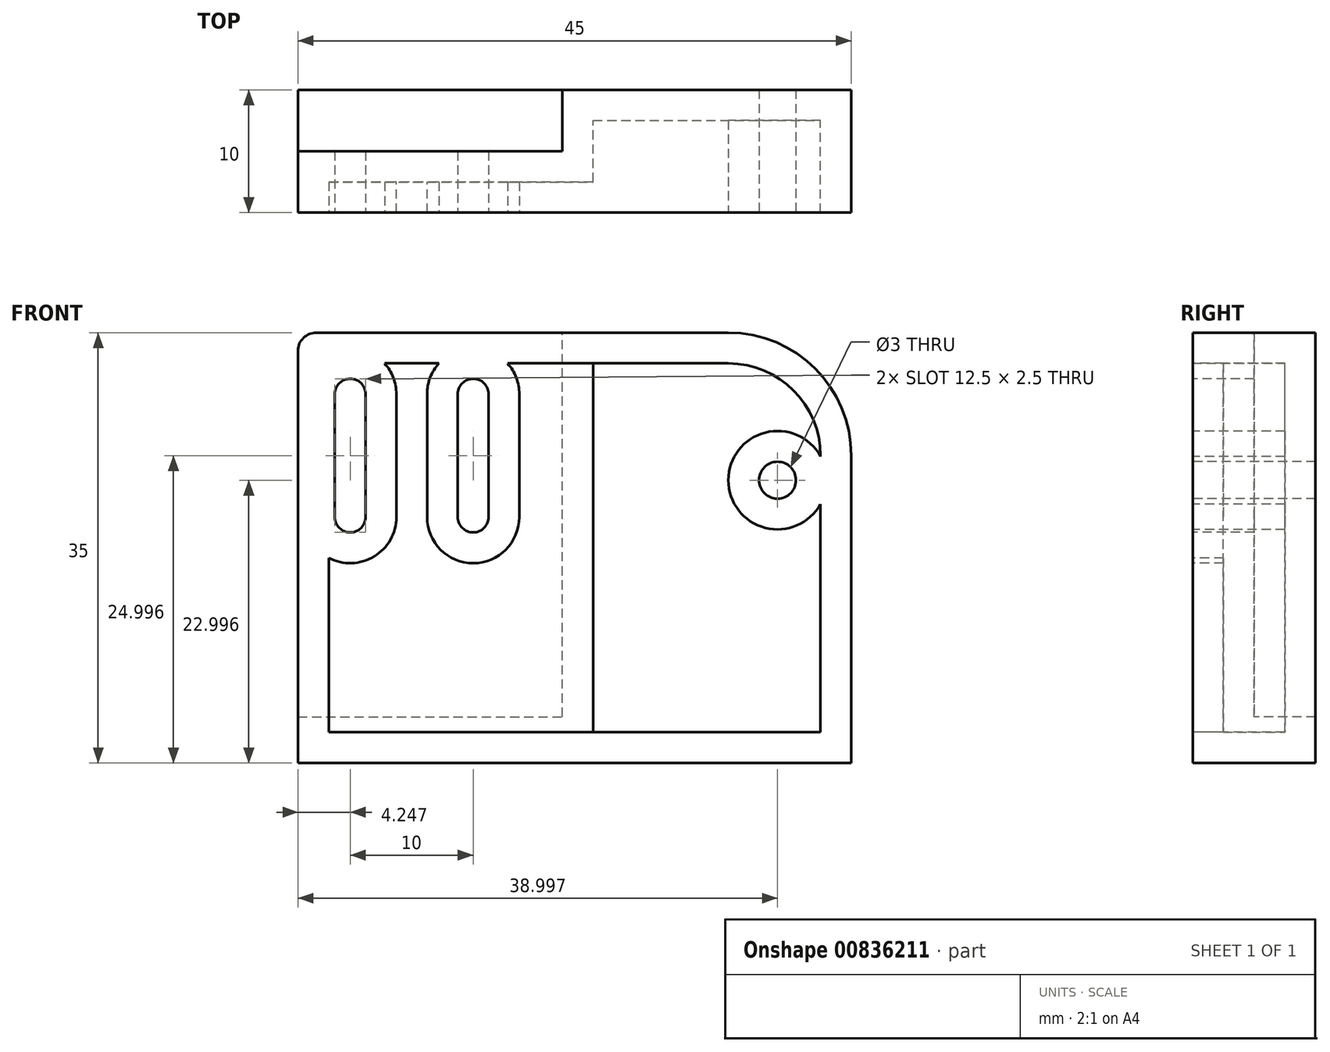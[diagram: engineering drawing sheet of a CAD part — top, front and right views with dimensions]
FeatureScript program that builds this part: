
annotation { "Feature Type Name" : "Feature", "Feature Type Description" : "" }
export const myFeature = defineFeature(function(context is Context, id is Id, definition is map)
    precondition{}
    {
        {
            var Q0;
            Q0=qCreatedBy(makeId("Front.planeOp"),FACE);
            var sketch = newSketch(context, id + "F0", { "sketchPlane" : qUnion([Q0])});
            skLineSegment(sketch, "E0.bottom", {"start": v(-19.85, 20.77) * mm, "end": v(25.15, 20.77) * mm});
            skLineSegment(sketch, "E0.top", {"start": v(-19.85, -14.23) * mm, "end": v(25.15, -14.23) * mm});
            skLineSegment(sketch, "E0.left", {"start": v(-19.85, 20.77) * mm, "end": v(-19.85, -14.23) * mm});
            skLineSegment(sketch, "E0.right", {"start": v(25.15, 20.77) * mm, "end": v(25.15, -14.23) * mm});
            skCircle(sketch, "E1", {"center": v(19.15, 8.77) * mm, "radius": 1.5 * mm});
            skCircle(sketch, "E2", {"center": v(-15.6, 15.77) * mm, "radius": 1.25 * mm});
            skCircle(sketch, "E3", {"center": v(-15.6, 5.77) * mm, "radius": 1.25 * mm});
            skLineSegment(sketch, "E4", {"start": v(-16.85, 15.77) * mm, "end": v(-16.85, 5.77) * mm});
            skLineSegment(sketch, "E5", {"start": v(-14.35, 15.77) * mm, "end": v(-14.35, 5.77) * mm});
            skCircle(sketch, "E6", {"center": v(-5.6, 15.77) * mm, "radius": 1.25 * mm});
            skCircle(sketch, "E7", {"center": v(-5.6, 5.77) * mm, "radius": 1.25 * mm});
            skLineSegment(sketch, "E8", {"start": v(-6.85, 15.77) * mm, "end": v(-6.85, 5.77) * mm});
            skLineSegment(sketch, "E9", {"start": v(-4.35, 15.77) * mm, "end": v(-4.35, 5.77) * mm});
            skLineSegment(sketch, "E10", {"start": v(-19.85, -10.48) * mm, "end": v(1.65, -10.48) * mm});
            skLineSegment(sketch, "E11", {"start": v(1.65, -10.48) * mm, "end": v(1.65, 20.77) * mm});
            skSolve(sketch);
        }
        {
            var Q0;
            {var subQ2=sQuery(id+"F0.wireOp",EDGE,"E0.top");Q0=makeQuery(id+"F0.imprint","IMPRINT",FACE,{"disambiguationData":[TD([[makeQuery(id+"F0.imprint","IMPRINT",EDGE,{"derivedFrom":subQ2}),1.0]])]});}
            extrude(context, id + "F1", {"entities" : qUnion([Q0]), "oppositeDirection" : true, "depth" : 10 * mm, "offsetDistance" : 25 * mm});
        }
        {
            var Q0;
            Q0=makeQuery(id+"F1.opExtrude","SWEPT_EDGE",EDGE,{"disambiguationData":[OSD([sQuery(id+"F0.wireOp",EDGE,"E0.bottom"),sQuery(id+"F0.wireOp",EDGE,"E0.right")])]});
            fillet(context, id + "F2", {"entities" : qUnion([Q0]), "radius" : 10 * mm, "tangentPropagation" : true, "allowEdgeOverflow" : false});
        }
        {
            var Q0;
            {var subQ5=sQuery(id+"F0.wireOp",EDGE,"E4");Q0=makeQuery(id+"F0.imprint","IMPRINT",FACE,{"disambiguationData":[TD([[makeQuery(id+"F0.imprint","IMPRINT",EDGE,{"derivedFrom":subQ5}),-1.0]])]});}
            extrude(context, id + "F3", {"entities" : qUnion([Q0]), "operationType" : NewBodyOperationType.ADD, "oppositeDirection" : true, "depth" : 5 * mm, "offsetDistance" : 25 * mm});
        }
        {
            var Q0;
            {var subQ0=sQuery(id+"F0.wireOp",EDGE,"E11");var subQ1=sQuery(id+"F0.wireOp",EDGE,"E10");var subQ2=sQuery(id+"F0.wireOp",EDGE,"E0.left");var subQ3=sQuery(id+"F0.wireOp",EDGE,"E0.bottom");Q0=makeQuery(id+"F3.boolean.opBoolean","MERGE",FACE,{"derivedFrom":[makeQuery(id+"F1.opExtrude","CAP_FACE",FACE,{"disambiguationData":[OSD([subQ3,sQuery(id+"F0.wireOp",EDGE,"E0.top"),subQ2,sQuery(id+"F0.wireOp",EDGE,"E0.right"),sQuery(id+"F0.wireOp",EDGE,"E1"),subQ1,subQ0])],"isStart":true}),makeQuery(id+"F3.opExtrude","CAP_FACE",FACE,{"disambiguationData":[OSD([subQ3,subQ2,sQuery(id+"F0.wireOp",EDGE,"E2"),sQuery(id+"F0.wireOp",EDGE,"E3"),sQuery(id+"F0.wireOp",EDGE,"E4"),sQuery(id+"F0.wireOp",EDGE,"E5"),sQuery(id+"F0.wireOp",EDGE,"E6"),sQuery(id+"F0.wireOp",EDGE,"E7"),sQuery(id+"F0.wireOp",EDGE,"E8"),sQuery(id+"F0.wireOp",EDGE,"E9"),subQ1,subQ0])],"isStart":true})]});}
            shell(context, id + "F4", {"entities" : qUnion([Q0]), "thickness" : 2.5 * mm});
        }
        {
            var Q0;
            Q0=makeQuery(id+"F3.opExtrude","SWEPT_EDGE",EDGE,{"disambiguationData":[OSD([sQuery(id+"F0.wireOp",EDGE,"E0.bottom"),sQuery(id+"F0.wireOp",EDGE,"E0.left")])]});
            fillet(context, id + "F5", {"entities" : qUnion([Q0]), "radius" : 1.5 * mm, "tangentPropagation" : true, "allowEdgeOverflow" : false});
        }
    });
